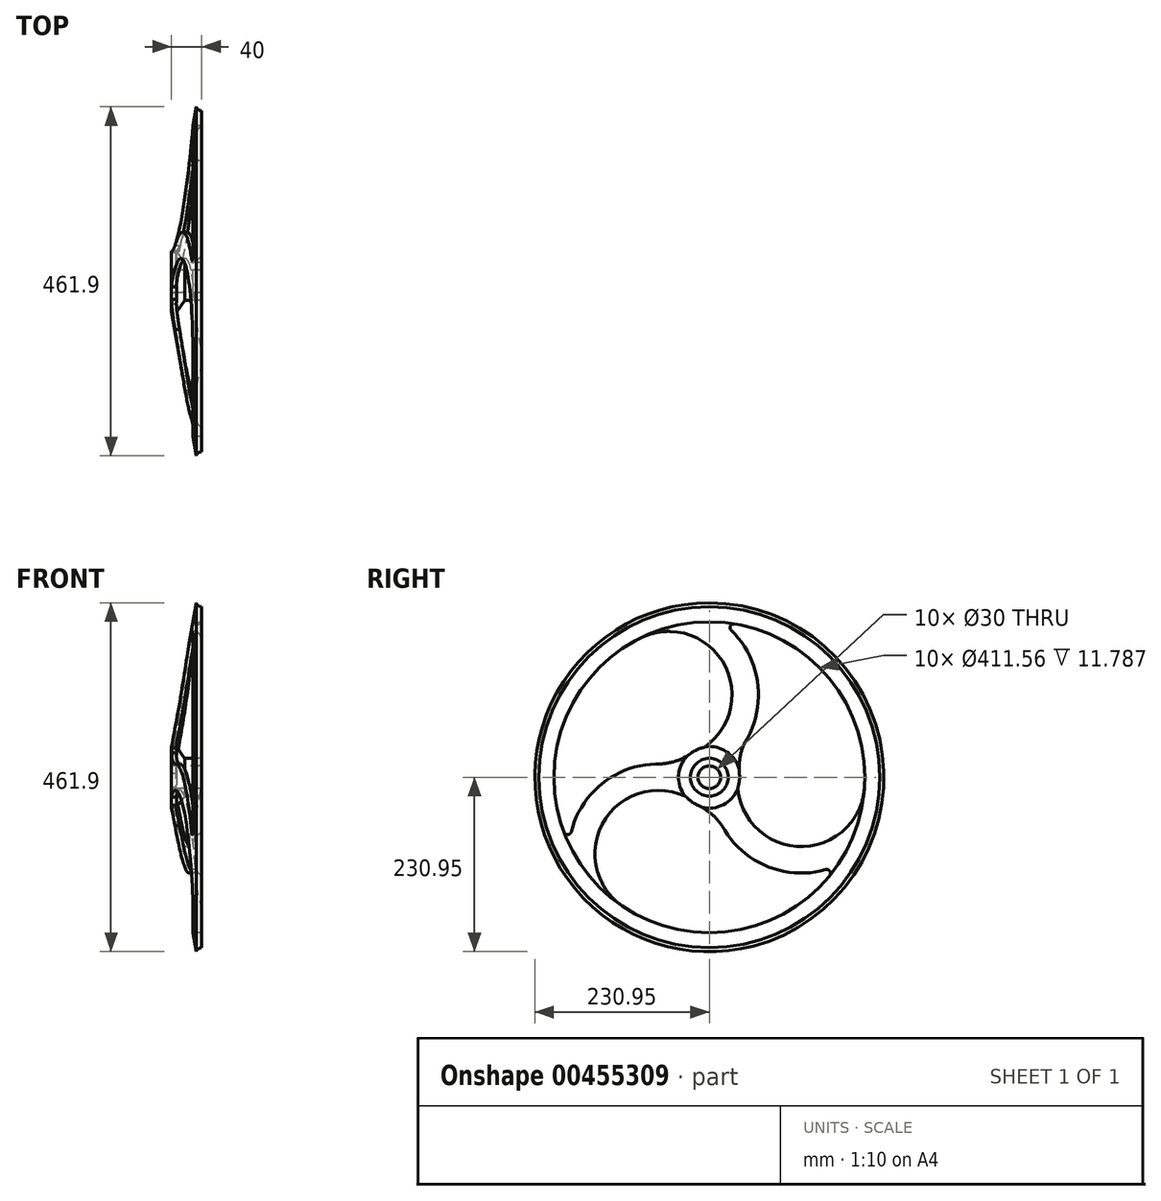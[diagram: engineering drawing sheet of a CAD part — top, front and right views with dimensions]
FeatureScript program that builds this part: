
annotation { "Feature Type Name" : "Feature", "Feature Type Description" : "" }
export const myFeature = defineFeature(function(context is Context, id is Id, definition is map)
    precondition{}
    {
        {
            var Q0;
            Q0=qCreatedBy(makeId("Front.planeOp"),FACE);
            cPlane(context, id + "F0", {"entities" : qUnion([Q0]), "cplaneType" : CPlaneType.OFFSET, "offset" : 0 * mm, "width" : 150 * mm, "height" : 150 * mm});
        }
        {
            var Q0;
            Q0=qCreatedBy(id+"F0.planeOp",FACE);
            var sketch = newSketch(context, id + "F1", { "sketchPlane" : qUnion([Q0])});
            skLineSegment(sketch, "E0.0", {"start": v(-33.77, 40.83) * mm, "end": v(-7.2, 199.97) * mm});
            skLineSegment(sketch, "E1.0", {"start": v(0, 205.78) * mm, "end": v(-1, 205.78) * mm});
            skPoint(sketch, "E1.1", {"position": v(-0.53, 205.78) * mm});
            skLineSegment(sketch, "E2.0", {"start": v(0, 225.73) * mm, "end": v(0, 205.78) * mm});
            skArc(sketch, "E3.0", {"start": v(-7.5, 230.95) * mm, "mid": v(-4.57, 227.16) * mm, "end": v(0, 225.73) * mm});
            skLineSegment(sketch, "E4", {"start": v(-7.5, 230.95) * mm, "end": v(-40, 40) * mm});
            skLineSegment(sketch, "E5.0", {"start": v(-40, 15) * mm, "end": v(-40, 40) * mm});
            skLineSegment(sketch, "E6.0", {"start": v(-33.77, 40.83) * mm, "end": v(-22.69, 25) * mm});
            skLineSegment(sketch, "E7.0", {"start": v(-22.69, 25) * mm, "end": v(0, 25) * mm});
            skLineSegment(sketch, "E8.0", {"start": v(0, 15) * mm, "end": v(-40, 15) * mm});
            skLineSegment(sketch, "E9.0", {"start": v(0, 15) * mm, "end": v(0, 25) * mm});
            skLineSegment(sketch, "E10", {"start": v(0, 233.73) * mm, "end": v(0, 0) * mm, "construction": true});
            skArc(sketch, "E11", {"start": v(-1, 205.78) * mm, "mid": v(-5.08, 203.92) * mm, "end": v(-7.2, 199.97) * mm});
            skLineSegment(sketch, "E12", {"start": v(-46.16, 0) * mm, "end": v(37.5, 0) * mm, "construction": true});
            skSolve(sketch);
        }
        {
            var Q0;
            Q0=qCreatedBy(makeId("Right.planeOp"),FACE);
            var sketch = newSketch(context, id + "F2", { "sketchPlane" : qUnion([Q0])});
            skCircle(sketch, "E13", {"center": v(0, 0) * mm, "radius": 233.73 * mm, "construction": true});
            skSolve(sketch);
        }
        {
            var Q0;
            Q0=makeQuery(id+"F1.imprint","IMPRINT",FACE,{"disambiguationData":[TD([[makeQuery(id+"F1.imprint","IMPRINT",EDGE,{"derivedFrom":sQuery(id+"F1.wireOp",EDGE,"E0.0")}),1.0]])]});
            var Q1;
            Q1=sQuery(id+"F2.wireOp",EDGE,"E13");
            revolve(context, id + "F3", {"entities" : qUnion([Q0]), "axis" : qUnion([Q1]), "revolveType" : RevolveType.FULL});
        }
        {
            var Q0;
            Q0=makeQuery(id+"F3.opRevolve","SWEPT_FACE",FACE,{"disambiguationData":[OSD([sQuery(id+"F1.wireOp",EDGE,"E5.0")])]});
            cPlane(context, id + "F4", {"entities" : qUnion([Q0]), "cplaneType" : CPlaneType.OFFSET, "offset" : 0 * mm, "width" : 150 * mm, "height" : 150 * mm});
        }
        {
            var Q0;
            Q0=qCreatedBy(id+"F4.planeOp",FACE);
            var sketch = newSketch(context, id + "F5", { "sketchPlane" : qUnion([Q0])});
            skArc(sketch, "E14.0", {"start": v(-39.7, 4.87) * mm, "mid": v(-39.76, -4.35) * mm, "end": v(-37.7, -13.35) * mm});
            skCircle(sketch, "E15.0", {"center": v(0, 0) * mm, "radius": 205.78 * mm, "construction": true});
            skArc(sketch, "E16", {"start": v(114.17, -171.2) * mm, "mid": v(140.33, -59.35) * mm, "end": v(30.42, -25.98) * mm});
            skArc(sketch, "E17.0", {"start": v(185.86, -88.33) * mm, "mid": v(145.66, -11.52) * mm, "end": v(64.01, 17.63) * mm});
            skArc(sketch, "E18", {"start": v(24.07, 31.95) * mm, "mid": v(43.04, 21.98) * mm, "end": v(64.01, 17.63) * mm});
            skLineSegment(sketch, "E19", {"start": v(0, 0) * mm, "end": v(88, 0) * mm, "construction": true});
            skLineSegment(sketch, "E20", {"start": v(0, 0) * mm, "end": v(24.07, 31.95) * mm, "construction": true});
            skLineSegment(sketch, "E21", {"start": v(0, 0) * mm, "end": v(30.42, -25.98) * mm, "construction": true});
            skArc(sketch, "E22.1.0", {"start": v(-39.7, 4.87) * mm, "mid": v(-40.56, 26.28) * mm, "end": v(-47.27, 46.62) * mm});
            skArc(sketch, "E22.1.1", {"start": v(-16.43, 205.12) * mm, "mid": v(-62.85, 131.9) * mm, "end": v(-47.27, 46.62) * mm});
            skArc(sketch, "E22.1.2", {"start": v(91.18, 184.48) * mm, "mid": v(-18.77, 151.2) * mm, "end": v(7.29, 39.33) * mm});
            skLineSegment(sketch, "E22.1.3", {"start": v(0, 0) * mm, "end": v(7.29, 39.33) * mm, "construction": true});
            skLineSegment(sketch, "E22.1.4", {"start": v(0, 0) * mm, "end": v(-39.7, 4.87) * mm, "construction": true});
            skArc(sketch, "E22.1.5", {"start": v(-39.7, 4.87) * mm, "mid": v(-35.8, -17.85) * mm, "end": v(-20, -34.64) * mm, "construction": true});
            skLineSegment(sketch, "E22.1.6", {"start": v(0, 0) * mm, "end": v(-44, 76.2) * mm, "construction": true});
            skArc(sketch, "E22.2.0", {"start": v(15.63, -36.82) * mm, "mid": v(-2.48, -48.26) * mm, "end": v(-16.74, -64.25) * mm});
            skArc(sketch, "E22.2.1", {"start": v(-169.43, -116.8) * mm, "mid": v(-82.8, -120.38) * mm, "end": v(-16.74, -64.25) * mm});
            skArc(sketch, "E22.2.2", {"start": v(-205.35, -13.28) * mm, "mid": v(-121.56, -91.86) * mm, "end": v(-37.7, -13.35) * mm});
            skLineSegment(sketch, "E22.2.3", {"start": v(0, 0) * mm, "end": v(-37.7, -13.35) * mm, "construction": true});
            skLineSegment(sketch, "E22.2.4", {"start": v(0, 0) * mm, "end": v(15.63, -36.82) * mm, "construction": true});
            skLineSegment(sketch, "E22.2.6", {"start": v(0, 0) * mm, "end": v(-44, -76.2) * mm, "construction": true});
            skArc(sketch, "E23", {"start": v(-16.43, 205.12) * mm, "mid": v(-155.63, 134.63) * mm, "end": v(-205.35, -13.28) * mm});
            skArc(sketch, "E24", {"start": v(-169.43, -116.8) * mm, "mid": v(-38.77, -202.1) * mm, "end": v(114.17, -171.2) * mm});
            skArc(sketch, "E25", {"start": v(185.86, -88.33) * mm, "mid": v(194.4, 67.47) * mm, "end": v(91.18, 184.48) * mm});
            skArc(sketch, "E26.trimOffspring", {"start": v(24.07, 31.95) * mm, "mid": v(16.1, 36.61) * mm, "end": v(7.29, 39.33) * mm});
            skArc(sketch, "E27.trimOffspring", {"start": v(15.63, -36.82) * mm, "mid": v(23.65, -32.26) * mm, "end": v(30.42, -25.98) * mm});
            skArc(sketch, "E28", {"start": v(-20, -34.64) * mm, "mid": v(30.75, 25.58) * mm, "end": v(-37.7, -13.35) * mm, "construction": true});
            skArc(sketch, "E29", {"start": v(134, -2.6) * mm, "mid": v(181.86, 17.22) * mm, "end": v(194.4, 67.47) * mm});
            skSolve(sketch);
        }
        {
            var Q0;
            Q0 = qSketchRegion(id + "F5", true);
            extrude(context, id + "F6", {"entities" : qUnion([Q0]), "operationType" : NewBodyOperationType.REMOVE, "oppositeDirection" : true, "depth" : 60 * mm, "offsetDistance" : 25 * mm});
        }
        {
            var Q0;
            Q0=makeQuery(id+"F6.boolean.opBoolean","COPY",EDGE,{"derivedFrom":makeQuery(id+"F6.opExtrude","SWEPT_EDGE",EDGE,{"disambiguationData":[OSD([sQuery(id+"F5.wireOp",EDGE,"E22.1.1"),sQuery(id+"F5.wireOp",EDGE,"E23")])]})});
            fillet(context, id + "F7", {"entities" : qUnion([Q0]), "radius" : 5 * mm, "tangentPropagation" : true, "allowEdgeOverflow" : false});
        }
        {
            var Q0;
            Q0=makeQuery(id+"F6.boolean.opBoolean","COPY",EDGE,{"derivedFrom":makeQuery(id+"F6.opExtrude","SWEPT_EDGE",EDGE,{"disambiguationData":[OSD([sQuery(id+"F5.wireOp",EDGE,"E22.2.1"),sQuery(id+"F5.wireOp",EDGE,"E24")])]})});
            fillet(context, id + "F8", {"entities" : qUnion([Q0]), "radius" : 5 * mm, "tangentPropagation" : true, "allowEdgeOverflow" : false});
        }
        {
            var Q0;
            Q0=makeQuery(id+"F6.boolean.opBoolean","COPY",EDGE,{"derivedFrom":makeQuery(id+"F6.opExtrude","SWEPT_EDGE",EDGE,{"disambiguationData":[OSD([sQuery(id+"F5.wireOp",EDGE,"E17.0"),sQuery(id+"F5.wireOp",EDGE,"E25")])]})});
            fillet(context, id + "F9", {"entities" : qUnion([Q0]), "radius" : 5 * mm, "tangentPropagation" : true, "allowEdgeOverflow" : false});
        }
    });
